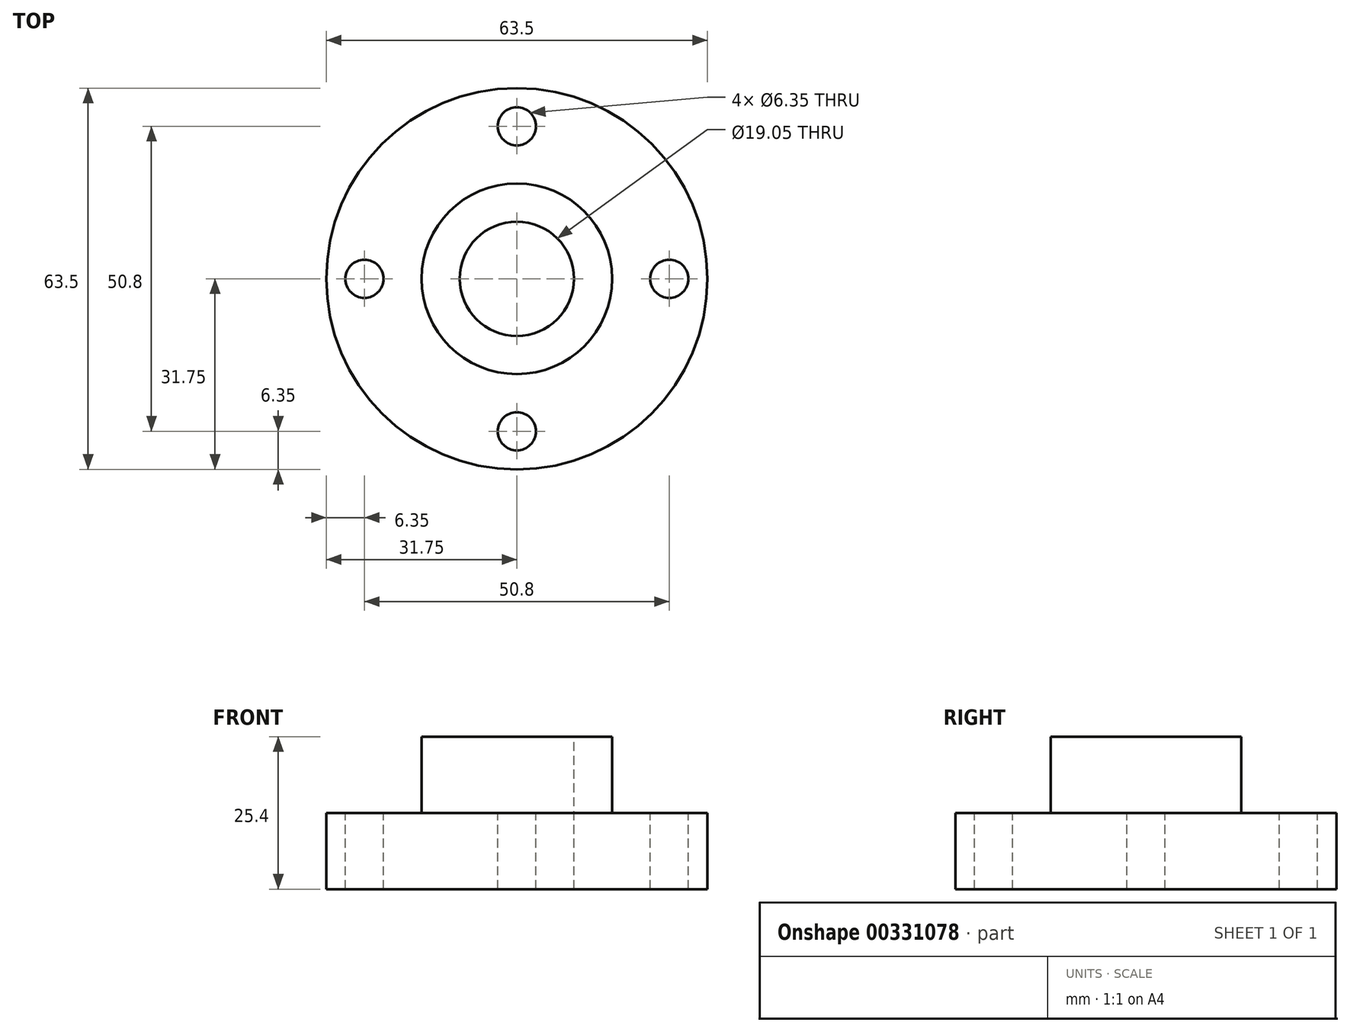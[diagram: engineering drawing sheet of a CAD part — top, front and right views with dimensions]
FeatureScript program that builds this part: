
annotation { "Feature Type Name" : "Feature", "Feature Type Description" : "" }
export const myFeature = defineFeature(function(context is Context, id is Id, definition is map)
    precondition{}
    {
        {
            var Q0;
            Q0=qCreatedBy(makeId("Top.planeOp"),FACE);
            var sketch = newSketch(context, id + "F0", { "sketchPlane" : qUnion([Q0])});
            skCircle(sketch, "E0", {"center": v(0, 0) * mm, "radius": 31.75 * mm});
            skSolve(sketch);
        }
        {
            var Q0;
            Q0 = qSketchRegion(id + "F0", true);
            extrude(context, id + "F1", {"entities" : qUnion([Q0]), "oppositeDirection" : true, "depth" : 12.7 * mm});
        }
        {
            var Q0;
            Q0=qCreatedBy(makeId("Top.planeOp"),FACE);
            var sketch = newSketch(context, id + "F2", { "sketchPlane" : qUnion([Q0])});
            skCircle(sketch, "E1", {"center": v(0, 0) * mm, "radius": 15.88 * mm});
            skSolve(sketch);
        }
        {
            var Q0;
            Q0 = qSketchRegion(id + "F2", true);
            extrude(context, id + "F3", {"entities" : qUnion([Q0]), "operationType" : NewBodyOperationType.ADD, "depth" : 12.7 * mm});
        }
        {
            var Q0;
            Q0=qCreatedBy(makeId("Top.planeOp"),FACE);
            var sketch = newSketch(context, id + "F4", { "sketchPlane" : qUnion([Q0])});
            skCircle(sketch, "E2", {"center": v(0, 0) * mm, "radius": 9.53 * mm});
            skCircle(sketch, "E3", {"center": v(0, 0) * mm, "radius": 25.4 * mm, "construction": true});
            skLineSegment(sketch, "E4", {"start": v(-46.45, 0) * mm, "end": v(59.53, 0) * mm, "construction": true});
            skLineSegment(sketch, "E5", {"start": v(0, -43.42) * mm, "end": v(0, 43.99) * mm, "construction": true});
            skCircle(sketch, "E6", {"center": v(0, 25.4) * mm, "radius": 3.18 * mm});
            skCircle(sketch, "E7", {"center": v(25.4, 0) * mm, "radius": 3.18 * mm});
            skCircle(sketch, "E8", {"center": v(0, -25.4) * mm, "radius": 3.18 * mm});
            skCircle(sketch, "E9", {"center": v(-25.4, 0) * mm, "radius": 3.18 * mm});
            skSolve(sketch);
        }
        {
            var Q0;
            Q0 = qSketchRegion(id + "F4", true);
            extrude(context, id + "F5", {"entities" : qUnion([Q0]), "operationType" : NewBodyOperationType.REMOVE, "endBound" : BoundingType.THROUGH_ALL, "oppositeDirection" : true, "depth" : 25.4 * mm, "hasSecondDirection" : true, "secondDirectionBound" : SecondDirectionBoundingType.THROUGH_ALL, "secondDirectionOppositeDirection" : false, "secondDirectionDepth" : 25.4 * mm});
        }
    });
